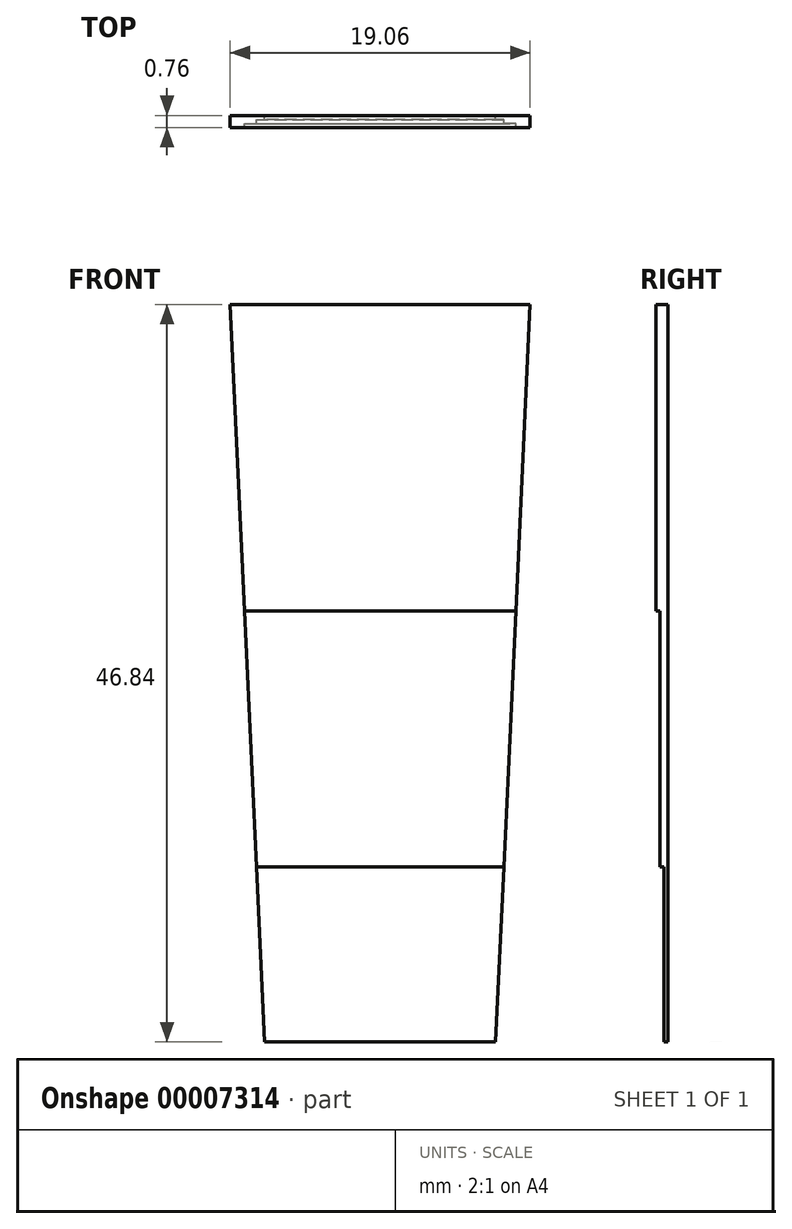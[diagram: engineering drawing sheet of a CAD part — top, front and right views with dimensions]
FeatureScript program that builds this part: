
annotation { "Feature Type Name" : "Feature", "Feature Type Description" : "" }
export const myFeature = defineFeature(function(context is Context, id is Id, definition is map)
    precondition{}
    {
        {
            var Q0;
            Q0=qCreatedBy(makeId("Front.planeOp"),FACE);
            var sketch = newSketch(context, id + "F0", { "sketchPlane" : qUnion([Q0])});
            skLineSegment(sketch, "E0", {"start": v(0, 0) * mm, "end": v(0, 46.84) * mm});
            skLineSegment(sketch, "E1", {"start": v(0, 46.84) * mm, "end": v(9.53, 46.84) * mm});
            skLineSegment(sketch, "E2", {"start": v(9.53, 46.84) * mm, "end": v(7.34, 0) * mm});
            skLineSegment(sketch, "E3", {"start": v(7.34, 0) * mm, "end": v(0, 0) * mm});
            skLineSegment(sketch, "E4", {"start": v(0, 11.13) * mm, "end": v(7.86, 11.13) * mm});
            skLineSegment(sketch, "E5", {"start": v(0, 27.38) * mm, "end": v(8.62, 27.38) * mm});
            skLineSegment(sketch, "E6.MirrorCS", {"start": v(0, 46.84) * mm, "end": v(-9.53, 46.84) * mm});
            skLineSegment(sketch, "E7.MirrorCS", {"start": v(-9.53, 46.84) * mm, "end": v(-7.34, 0) * mm});
            skLineSegment(sketch, "E8.MirrorCS", {"start": v(0, 27.38) * mm, "end": v(-8.62, 27.38) * mm});
            skLineSegment(sketch, "E9.MirrorCS", {"start": v(0, 11.13) * mm, "end": v(-7.86, 11.13) * mm});
            skLineSegment(sketch, "E10.MirrorCS", {"start": v(-7.34, 0) * mm, "end": v(0, 0) * mm});
            skSolve(sketch);
        }
        {
            var Q0;
            {var subQ0=sQuery(id+"F0.wireOp",EDGE,"E3");Q0=makeQuery(id+"F0.imprint","IMPRINT",FACE,{"disambiguationData":[TD([[makeQuery(id+"F0.imprint","IMPRINT",EDGE,{"derivedFrom":subQ0}),-1.0]])]});}
            var Q1;
            {var subQ2=sQuery(id+"F0.wireOp",EDGE,"E9.MirrorCS");Q1=makeQuery(id+"F0.imprint","IMPRINT",FACE,{"disambiguationData":[TD([[makeQuery(id+"F0.imprint","IMPRINT",EDGE,{"derivedFrom":subQ2}),1.0]])]});}
            extrude(context, id + "F1", {"entities" : qUnion([Q0, Q1]), "depth" : 0.25 * mm});
        }
        {
            var Q0;
            {var subQ0=sQuery(id+"F0.wireOp",EDGE,"E4");Q0=makeQuery(id+"F0.imprint","IMPRINT",FACE,{"disambiguationData":[TD([[makeQuery(id+"F0.imprint","IMPRINT",EDGE,{"derivedFrom":subQ0}),1.0]])]});}
            var Q1;
            {var subQ2=sQuery(id+"F0.wireOp",EDGE,"E8.MirrorCS");Q1=makeQuery(id+"F0.imprint","IMPRINT",FACE,{"disambiguationData":[TD([[makeQuery(id+"F0.imprint","IMPRINT",EDGE,{"derivedFrom":subQ2}),1.0]])]});}
            extrude(context, id + "F2", {"entities" : qUnion([Q0, Q1]), "operationType" : NewBodyOperationType.ADD, "depth" : 0.5 * mm});
        }
        {
            var Q0;
            {var subQ0=sQuery(id+"F0.wireOp",EDGE,"E1");Q0=makeQuery(id+"F0.imprint","IMPRINT",FACE,{"disambiguationData":[TD([[makeQuery(id+"F0.imprint","IMPRINT",EDGE,{"derivedFrom":subQ0}),-1.0]])]});}
            var Q1;
            {var subQ0=sQuery(id+"F0.wireOp",EDGE,"E6.MirrorCS");Q1=makeQuery(id+"F0.imprint","IMPRINT",FACE,{"disambiguationData":[TD([[makeQuery(id+"F0.imprint","IMPRINT",EDGE,{"derivedFrom":subQ0}),1.0]])]});}
            extrude(context, id + "F3", {"entities" : qUnion([Q0, Q1]), "operationType" : NewBodyOperationType.ADD, "depth" : 0.76 * mm});
        }
    });
